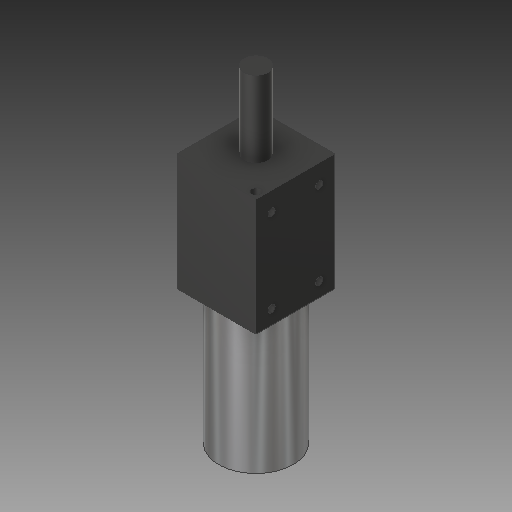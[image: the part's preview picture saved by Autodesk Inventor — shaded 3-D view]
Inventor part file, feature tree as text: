
AUTODESK INVENTOR PART (.ipt)
format: ipt  version: 2017 SP1 (Build 210196100, 196)  size: 139,264 bytes
history: native  units: in
note: dims shown in document units (in); Inventor stores cm internally (conversion verified against a paired STEP export)
features: extrude x5, sketch x5
ambient origin geometry x8: Origin, YZ Plane, XZ Plane, XY Plane, X Axis, Y Axis, Z Axis, Center Point
bodies: Solid1 (feature_tree)
feature tree (10):
  extrude  "Extrusion1"  Depth=1.65in
  extrude  "Extrusion2"  Depth=2.45in TaperAngle=0.0deg
  extrude  "Extrusion3"  Depth=2.8in TaperAngle=0.0deg
  extrude  "Extrusion4"  Depth=0.06in TaperAngle=0.0deg
  extrude  "Extrusion5"  Depth=1.6in TaperAngle=0.0deg
  sketch  "Sketch1"  dims[d0=1.65in d1=1.375in]
  sketch  "Sketch2"  dims[d2=0.2in d3=2.45in d4=0.0in]
  sketch  "Sketch3"  dims[d5=1.56in d6=2.8in d7=0.0in]
  sketch  "Sketch4"  dims[d8=0.5in d9=0.06in d10=0.0in]
  sketch  "Sketch5"  dims[d11=0.5in d12=1.6in d13=0.0in d14=1.0in d15=1.75in d16=0.4in d17=0.15in d18=1.6in d19=0.0in]
